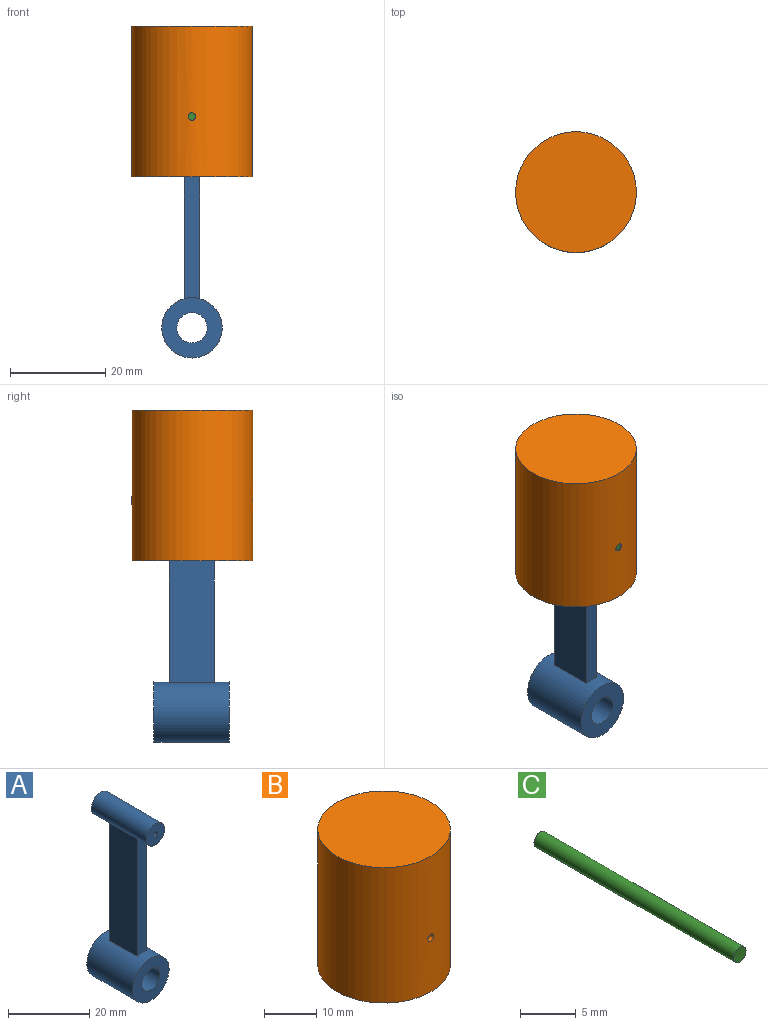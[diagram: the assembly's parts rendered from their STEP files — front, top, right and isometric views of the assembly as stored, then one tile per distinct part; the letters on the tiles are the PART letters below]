
ASSEMBLY  parts=3 mates=2
PART A: 12 faces, bbox 12.7x19.1x54 mm
  f0: plane 35.55x3.18mm, normal (0,-1,0), area 111.5mm2, adj f2,f6,f7,f9
  f1: plane 35.55x3.18mm, normal (0,1,0), area 111.5mm2, adj f2,f6,f7,f9
  f2: cylinder r=6.35mm len=15.88mm, axis (0,-1,0), area 602.8mm2, adj f0,f1,f3,f5,f6,f7
  f3: plane 12.7x12.7mm, normal (0,-1,0), area 95mm2, adj f2,f4
  f4: cylinder r=3.17mm len=15.88mm, axis (0,-1,0), area 316.7mm2, adj f3,f5
  f5: plane 12.7x12.7mm, normal (0,1,0), area 95mm2, adj f2,f4
  f6: plane 35.55x9.53mm, normal (1,0,0), area 338.6mm2, adj f0,f1,f2,f9
  f7: plane 35.55x9.53mm, normal (-1,0,0), area 338.6mm2, adj f0,f1,f2,f9
  f8: plane 6.35x6.35mm, normal (0,1,0), area 29.7mm2, adj f9,f11
  f9: cylinder r=3.17mm len=19.05mm, axis (0,-1,0), area 348.4mm2, adj f0,f1,f6,f7,f8,f10
  f10: plane 6.35x6.35mm, normal (0,-1,0), area 29.7mm2, adj f9,f11
  f11: cylinder r=0.79mm len=19.05mm, axis (0,-1,0), area 95mm2, adj f8,f10
PART B: 7 faces, bbox 25.4x25.4x31.8 mm
  f0: cylinder r=9.53mm len=25.4mm, axis (0,0,1), area 1516.2mm2, adj f2,f4,f5,f6
  f1: cylinder r=12.7mm len=31.75mm, axis (0,0,1), area 2529.6mm2, adj f3,f4,f5,f6
  f2: plane 19.05x19.05mm, normal (0,0,-1), area 285mm2, adj f0
  f3: plane 25.4x25.4mm, normal (0,0,1), area 506.7mm2, adj f1
  f4: cone r=9.53mm half-angle=45deg, axis (0,0,-1), area 313.5mm2, adj f0,f1
  f5: cylinder r=0.79mm len=3.21mm, axis (0,1,0), area 15.9mm2, adj f0,f1
  f6: cylinder r=0.79mm len=3.21mm, axis (0,1,0), area 15.9mm2, adj f0,f1
PART C: 3 faces, bbox 1.6x25.4x1.6 mm
  f0: cylinder r=12.7mm len=1.59mm, axis (0,0,1), area 2mm2, adj f2
  f1: cylinder r=12.7mm len=1.59mm, axis (0,0,1), area 2mm2, adj f2
  f2: cylinder r=0.79mm len=25.4mm, axis (0,-1,0), area 126.6mm2, adj f0,f1
PLACE A t=(-24.01,-24.34,-6.73)mm
PLACE B t=(-24.01,-24.47,-6.73)mm
PLACE C t=(-24.01,-24.34,-6.73)mm
MATE revolute B.f5 <-> C.f2  axis (0,1,0) through (-24.01,-52.13,50.42)mm
MATE revolute C.f2 <-> A.f9  axis (0,-1,0) through (-24.01,-39.28,50.42)mm
